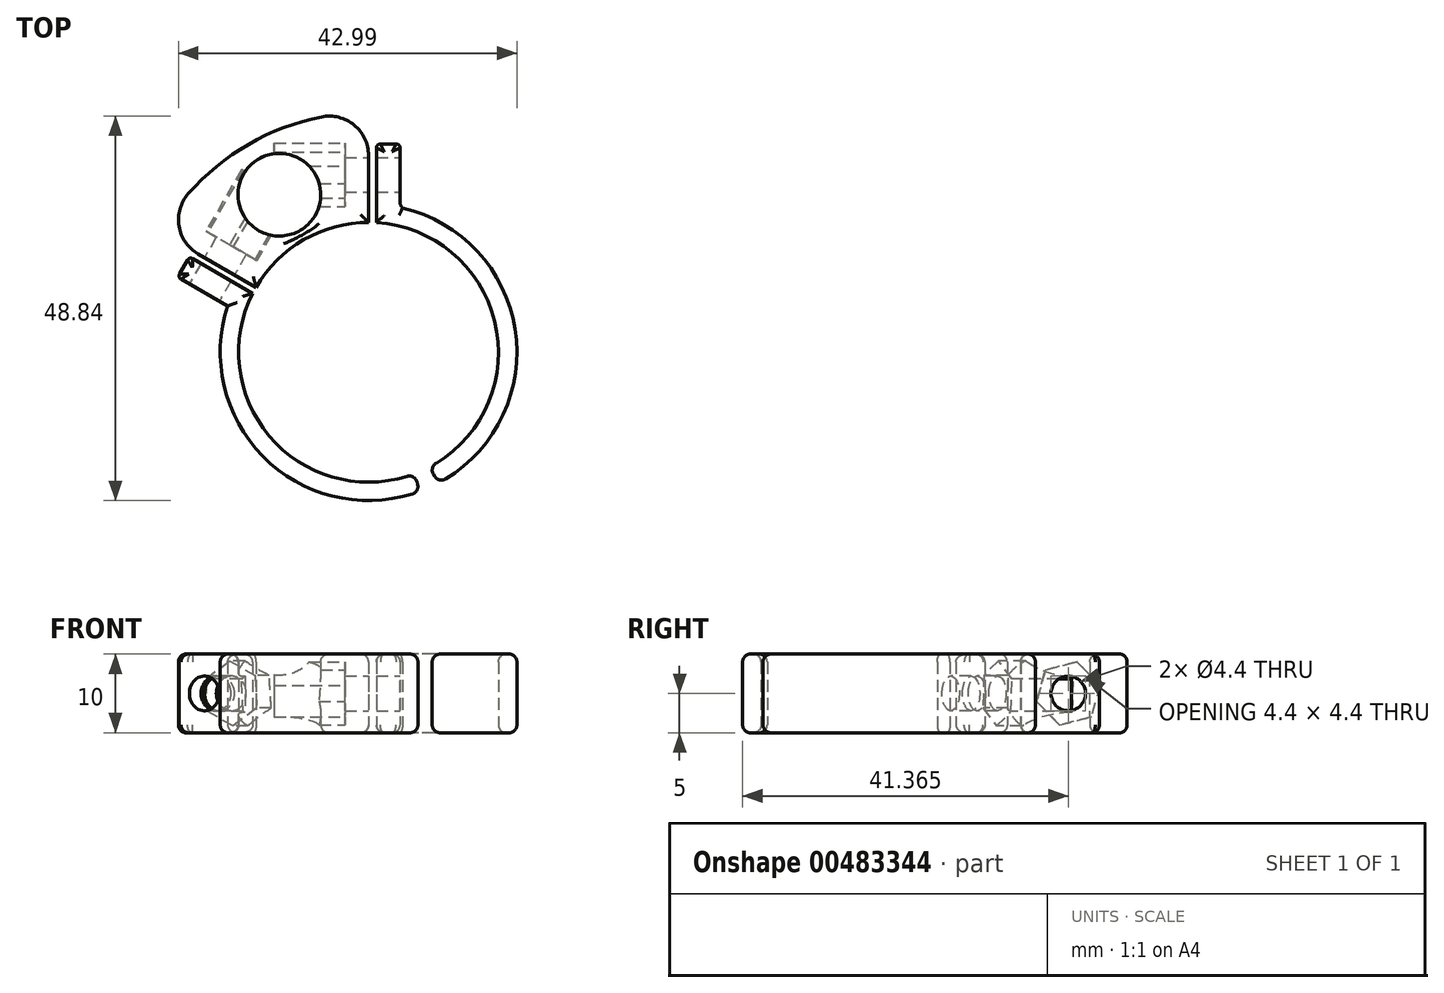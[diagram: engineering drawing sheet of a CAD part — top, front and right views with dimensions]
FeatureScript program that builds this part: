
annotation { "Feature Type Name" : "Feature", "Feature Type Description" : "" }
export const myFeature = defineFeature(function(context is Context, id is Id, definition is map)
    precondition{}
    {
        {
            var Q0;
            Q0=qCreatedBy(makeId("Top.planeOp"),FACE);
            var sketch = newSketch(context, id + "F0", { "sketchPlane" : qUnion([Q0])});
            skLineSegment(sketch, "E0", {"start": v(0, 18.5) * mm, "end": v(0, 18.5) * mm});
            skArc(sketch, "E1", {"start": v(-22.9, 20.13) * mm, "mid": v(-15.25, 26.41) * mm, "end": v(-5.98, 29.9) * mm});
            skLineSegment(sketch, "E2", {"start": v(0, 18.5) * mm, "end": v(0, 25) * mm});
            skLineSegment(sketch, "E3", {"start": v(0, 0) * mm, "end": v(-21.65, 12.5) * mm});
            skLineSegment(sketch, "E4", {"start": v(0, 18.5) * mm, "end": v(0, 24.5) * mm});
            skCircle(sketch, "E5", {"center": v(-11.33, 20.01) * mm, "radius": 5.25 * mm});
            skLineSegment(sketch, "E6", {"start": v(1, 18.47) * mm, "end": v(1, 18.47) * mm});
            skLineSegment(sketch, "E7", {"start": v(1, 18.47) * mm, "end": v(1, 25.97) * mm});
            skLineSegment(sketch, "E8", {"start": v(0, 16.5) * mm, "end": v(0, 18.5) * mm});
            skLineSegment(sketch, "E9", {"start": v(1, 18.47) * mm, "end": v(1, 16.47) * mm});
            skArc(sketch, "E10", {"start": v(0, 16.5) * mm, "mid": v(-8.25, 14.29) * mm, "end": v(-14.29, 8.25) * mm});
            skLineSegment(sketch, "E11", {"start": v(1.5, 26.47) * mm, "end": v(3.5, 26.47) * mm});
            skLineSegment(sketch, "E12", {"start": v(4, 25.97) * mm, "end": v(4, 19.08) * mm});
            skLineSegment(sketch, "E13", {"start": v(-14.7, 7.5) * mm, "end": v(-22.32, 11.9) * mm});
            skLineSegment(sketch, "E14", {"start": v(-23, 11.71) * mm, "end": v(-24, 9.98) * mm});
            skLineSegment(sketch, "E15", {"start": v(-23.82, 9.3) * mm, "end": v(-17.9, 5.88) * mm});
            skPoint(sketch, "E16.visualSharp", {"position": v(-26.41, 15.25) * mm});
            skArc(sketch, "E16.filletArc", {"start": v(-22.9, 20.13) * mm, "mid": v(-24.08, 16.02) * mm, "end": v(-21.65, 12.5) * mm});
            skPoint(sketch, "E17.visualSharp", {"position": v(0, 30.5) * mm});
            skArc(sketch, "E17.filletArc", {"start": v(0, 25) * mm, "mid": v(-1.83, 28.87) * mm, "end": v(-5.98, 29.9) * mm});
            skPoint(sketch, "E18.visualSharp", {"position": v(1, 26.47) * mm});
            skArc(sketch, "E18.filletArc", {"start": v(1.5, 26.47) * mm, "mid": v(1.15, 26.32) * mm, "end": v(1, 25.97) * mm});
            skPoint(sketch, "E19.visualSharp", {"position": v(4, 26.47) * mm});
            skArc(sketch, "E19.filletArc", {"start": v(4, 25.97) * mm, "mid": v(3.85, 26.32) * mm, "end": v(3.5, 26.47) * mm});
            skPoint(sketch, "E20.visualSharp", {"position": v(-24.26, 9.55) * mm});
            skArc(sketch, "E20.filletArc", {"start": v(-24, 9.98) * mm, "mid": v(-24.06, 9.6) * mm, "end": v(-23.82, 9.3) * mm});
            skPoint(sketch, "E21.visualSharp", {"position": v(-22.76, 12.14) * mm});
            skArc(sketch, "E21.filletArc", {"start": v(-22.32, 11.9) * mm, "mid": v(-22.7, 11.94) * mm, "end": v(-23, 11.71) * mm});
            skPoint(sketch, "E22.visualSharp", {"position": v(4, 18.25) * mm});
            skArc(sketch, "E22.filletArc", {"start": v(4, 19.08) * mm, "mid": v(4.22, 18.45) * mm, "end": v(4.8, 18.1) * mm});
            skLineSegment(sketch, "E23", {"start": v(8.9, -16.6) * mm, "end": v(7.7, -14.59) * mm});
            skLineSegment(sketch, "E24", {"start": v(5.85, -15.43) * mm, "end": v(6.49, -17.7) * mm});
            skArc(sketch, "E25", {"start": v(-17.9, 5.88) * mm, "mid": v(-13.1, -13.55) * mm, "end": v(6.49, -17.7) * mm});
            skArc(sketch, "E26.trimOffspring", {"start": v(8.9, -16.6) * mm, "mid": v(18.68, 2.45) * mm, "end": v(4.33, 18.34) * mm});
            skArc(sketch, "E27", {"start": v(1, 16.47) * mm, "mid": v(16.13, 3.48) * mm, "end": v(7.7, -14.59) * mm});
            skArc(sketch, "E28", {"start": v(5.85, -15.43) * mm, "mid": v(-12.29, -11.01) * mm, "end": v(-14.7, 7.5) * mm});
            skSolve(sketch);
        }
        {
            var Q0;
            Q0=qSketchRegion(id+"F0",true);
            extrude(context, id + "F1", {"entities" : qUnion([Q0]), "depth" : 10 * mm});
        }
        {
            var Q0;
            Q0=makeQuery(id+"F1.opExtrude","SWEPT_FACE",FACE,{"disambiguationData":[OSD([sQuery(id+"F0.wireOp",EDGE,"E12")])]});
            var sketch = newSketch(context, id + "F2", { "sketchPlane" : qUnion([Q0])});
            skCircle(sketch, "E29", {"center": v(22.52, 5) * mm, "radius": 2.2 * mm});
            skPoint(sketch, "E29.centerSnap0", {"position": v(22.52, 0) * mm});
            skPoint(sketch, "E29.centerSnap1", {"position": v(19.08, 5) * mm});
            skSolve(sketch);
        }
        {
            var Q0;
            Q0=qSketchRegion(id+"F2",true);
            extrude(context, id + "F3", {"entities" : qUnion([Q0]), "operationType" : NewBodyOperationType.REMOVE, "oppositeDirection" : true, "depth" : 8 * mm});
        }
        {
            var Q0;
            Q0=makeQuery(id+"F1.opExtrude","SWEPT_FACE",FACE,{"disambiguationData":[OSD([sQuery(id+"F0.wireOp",EDGE,"E15")])]});
            var sketch = newSketch(context, id + "F4", { "sketchPlane" : qUnion([Q0])});
            skCircle(sketch, "E30", {"center": v(-21.86, 5) * mm, "radius": 2.2 * mm});
            skPoint(sketch, "E30.centerSnap0", {"position": v(-21.86, 10) * mm});
            skPoint(sketch, "E30.centerSnap1", {"position": v(-25.28, 5) * mm});
            skSolve(sketch);
        }
        {
            var Q0;
            Q0=makeQuery(id+"F4.imprint","IMPRINT",FACE,{"disambiguationData":[TD([[makeQuery(id+"F4.imprint","IMPRINT",EDGE,{"derivedFrom":sQuery(id+"F4.wireOp",EDGE,"E30")}),1.0]])]});
            extrude(context, id + "F5", {"entities" : qUnion([Q0]), "operationType" : NewBodyOperationType.REMOVE, "oppositeDirection" : true, "depth" : 10 * mm});
        }
        {
            var Q0;
            Q0=makeQuery(id+"F1.opExtrude","SWEPT_FACE",FACE,{"disambiguationData":[OSD([sQuery(id+"F0.wireOp",EDGE,"E3")])]});
            var sketch = newSketch(context, id + "F6", { "sketchPlane" : qUnion([Q0])});
            skCircle(sketch, "E31.cCircle", {"center": v(-21.86, 5) * mm, "radius": 3.6 * mm, "construction": true});
            skLineSegment(sketch, "E31.0", {"start": v(-22.11, 9.15) * mm, "end": v(-18.4, 7.3) * mm});
            skLineSegment(sketch, "E31.1", {"start": v(-18.4, 7.3) * mm, "end": v(-18.14, 3.14) * mm});
            skLineSegment(sketch, "E31.2", {"start": v(-18.14, 3.14) * mm, "end": v(-21.6, 0.85) * mm});
            skLineSegment(sketch, "E31.3", {"start": v(-21.6, 0.85) * mm, "end": v(-25.33, 2.7) * mm});
            skLineSegment(sketch, "E31.4", {"start": v(-25.33, 2.7) * mm, "end": v(-25.58, 6.86) * mm});
            skLineSegment(sketch, "E31.5", {"start": v(-25.58, 6.86) * mm, "end": v(-22.11, 9.15) * mm});
            skPoint(sketch, "E31.0.midPoint", {"position": v(-20.25, 8.22) * mm});
            skSolve(sketch);
        }
        {
            var Q0;
            Q0=makeQuery(id+"F6.imprint","IMPRINT",FACE,{"disambiguationData":[TD([[makeQuery(id+"F6.imprint","IMPRINT",EDGE,{"derivedFrom":makeQuery(id+"F5.boolean.opBoolean","INTERSECT",EDGE,{"derivedFrom":[makeQuery(id+"F1.opExtrude","SWEPT_FACE",FACE,{"disambiguationData":[OSD([sQuery(id+"F0.wireOp",EDGE,"E3")])]}),makeQuery(id+"F5.opExtrude","SWEPT_FACE",FACE,{"disambiguationData":[OSD([sQuery(id+"F4.wireOp",EDGE,"E30")])]})]})}),1.0]])]});
            var Q1;
            {var subQ0=sQuery(id+"F6.wireOp",EDGE,"E31.4");Q1=makeQuery(id+"F6.imprint","IMPRINT",FACE,{"disambiguationData":[TD([[makeQuery(id+"F6.imprint","IMPRINT",EDGE,{"derivedFrom":subQ0}),-1.0]])]});}
            var Q2;
            {var subQ7=sQuery(id+"F6.wireOp",EDGE,"E31.0");Q2=makeQuery(id+"F6.imprint","IMPRINT",FACE,{"disambiguationData":[TD([[makeQuery(id+"F6.imprint","IMPRINT",EDGE,{"derivedFrom":subQ7}),-1.0]])]});}
            extrude(context, id + "F7", {"entities" : qUnion([Q0, Q1, Q2]), "operationType" : NewBodyOperationType.REMOVE, "oppositeDirection" : true, "depth" : 12 * mm, "hasSecondDirection" : true, "secondDirectionOppositeDirection" : true, "secondDirectionDepth" : 3 * mm});
        }
        {
            var Q0;
            Q0=makeQuery(id+"F1.opExtrude","SWEPT_FACE",FACE,{"disambiguationData":[OSD([sQuery(id+"F0.wireOp",EDGE,"E2"),sQuery(id+"F0.wireOp",EDGE,"E4"),sQuery(id+"F0.wireOp",EDGE,"E8")])]});
            var sketch = newSketch(context, id + "F8", { "sketchPlane" : qUnion([Q0])});
            skCircle(sketch, "E32.cCircle", {"center": v(22.52, 5) * mm, "radius": 3.6 * mm, "construction": true});
            skLineSegment(sketch, "E32.0", {"start": v(19.62, 7.97) * mm, "end": v(23.64, 9) * mm});
            skLineSegment(sketch, "E32.1", {"start": v(23.64, 9) * mm, "end": v(26.55, 6.03) * mm});
            skLineSegment(sketch, "E32.2", {"start": v(26.55, 6.03) * mm, "end": v(25.43, 2.03) * mm});
            skLineSegment(sketch, "E32.3", {"start": v(25.43, 2.03) * mm, "end": v(21.4, 1) * mm});
            skLineSegment(sketch, "E32.4", {"start": v(21.4, 1) * mm, "end": v(18.5, 3.97) * mm});
            skLineSegment(sketch, "E32.5", {"start": v(18.5, 3.97) * mm, "end": v(19.62, 7.97) * mm});
            skPoint(sketch, "E32.0.midPoint", {"position": v(21.63, 8.49) * mm});
            skSolve(sketch);
        }
        {
            var Q0;
            Q0=qSketchRegion(id+"F8",true);
            extrude(context, id + "F9", {"entities" : qUnion([Q0]), "operationType" : NewBodyOperationType.REMOVE, "oppositeDirection" : true, "depth" : 12 * mm, "hasSecondDirection" : true, "secondDirectionOppositeDirection" : true, "secondDirectionDepth" : 3 * mm});
        }
        {
            var Q0;
            Q0=makeQuery(id+"F1.opExtrude","SWEPT_FACE",FACE,{"disambiguationData":[OSD([sQuery(id+"F0.wireOp",EDGE,"E24")])]});
            var Q1;
            Q1=makeQuery(id+"F1.opExtrude","SWEPT_FACE",FACE,{"disambiguationData":[OSD([sQuery(id+"F0.wireOp",EDGE,"E23")])]});
            var Q2;
            Q2=makeQuery(id+"F1.opExtrude","CAP_FACE",FACE,{"disambiguationData":[OSD([sQuery(id+"F0.wireOp",EDGE,"E13"),sQuery(id+"F0.wireOp",EDGE,"E14"),sQuery(id+"F0.wireOp",EDGE,"E15"),sQuery(id+"F0.wireOp",EDGE,"E20.filletArc"),sQuery(id+"F0.wireOp",EDGE,"E21.filletArc"),sQuery(id+"F0.wireOp",EDGE,"E24"),sQuery(id+"F0.wireOp",EDGE,"E25"),sQuery(id+"F0.wireOp",EDGE,"a188417b-cc8c-4509-bfe6-a5d54d56d6b7.trimOffspring")])],"isStart":false});
            var Q3;
            Q3=makeQuery(id+"F1.opExtrude","CAP_FACE",FACE,{"disambiguationData":[OSD([sQuery(id+"F0.wireOp",EDGE,"E7"),sQuery(id+"F0.wireOp",EDGE,"E9"),sQuery(id+"F0.wireOp",EDGE,"E11"),sQuery(id+"F0.wireOp",EDGE,"E12"),sQuery(id+"F0.wireOp",EDGE,"E18.filletArc"),sQuery(id+"F0.wireOp",EDGE,"E19.filletArc"),sQuery(id+"F0.wireOp",EDGE,"E22.filletArc"),sQuery(id+"F0.wireOp",EDGE,"E23"),sQuery(id+"F0.wireOp",EDGE,"jDdMIHg0-1Oi0-MaQn-ggq3-3935tTYizpBS"),sQuery(id+"F0.wireOp",EDGE,"E26.trimOffspring")])],"isStart":false});
            var Q4;
            Q4=makeQuery(id+"F1.opExtrude","CAP_FACE",FACE,{"disambiguationData":[OSD([sQuery(id+"F0.wireOp",EDGE,"E1"),sQuery(id+"F0.wireOp",EDGE,"E2"),sQuery(id+"F0.wireOp",EDGE,"E3"),sQuery(id+"F0.wireOp",EDGE,"E4"),sQuery(id+"F0.wireOp",EDGE,"E5"),sQuery(id+"F0.wireOp",EDGE,"E8"),sQuery(id+"F0.wireOp",EDGE,"E10"),sQuery(id+"F0.wireOp",EDGE,"E16.filletArc"),sQuery(id+"F0.wireOp",EDGE,"E17.filletArc")])],"isStart":false});
            var Q5;
            Q5=makeQuery(id+"F1.opExtrude","CAP_FACE",FACE,{"disambiguationData":[OSD([sQuery(id+"F0.wireOp",EDGE,"E1"),sQuery(id+"F0.wireOp",EDGE,"E2"),sQuery(id+"F0.wireOp",EDGE,"E3"),sQuery(id+"F0.wireOp",EDGE,"E4"),sQuery(id+"F0.wireOp",EDGE,"E5"),sQuery(id+"F0.wireOp",EDGE,"E8"),sQuery(id+"F0.wireOp",EDGE,"E10"),sQuery(id+"F0.wireOp",EDGE,"E16.filletArc"),sQuery(id+"F0.wireOp",EDGE,"E17.filletArc")])],"isStart":true});
            var Q6;
            Q6=makeQuery(id+"F1.opExtrude","CAP_FACE",FACE,{"disambiguationData":[OSD([sQuery(id+"F0.wireOp",EDGE,"E7"),sQuery(id+"F0.wireOp",EDGE,"E9"),sQuery(id+"F0.wireOp",EDGE,"E11"),sQuery(id+"F0.wireOp",EDGE,"E12"),sQuery(id+"F0.wireOp",EDGE,"E18.filletArc"),sQuery(id+"F0.wireOp",EDGE,"E19.filletArc"),sQuery(id+"F0.wireOp",EDGE,"E22.filletArc"),sQuery(id+"F0.wireOp",EDGE,"E23"),sQuery(id+"F0.wireOp",EDGE,"jDdMIHg0-1Oi0-MaQn-ggq3-3935tTYizpBS"),sQuery(id+"F0.wireOp",EDGE,"E26.trimOffspring")])],"isStart":true});
            var Q7;
            Q7=makeQuery(id+"F1.opExtrude","CAP_FACE",FACE,{"disambiguationData":[OSD([sQuery(id+"F0.wireOp",EDGE,"E13"),sQuery(id+"F0.wireOp",EDGE,"E14"),sQuery(id+"F0.wireOp",EDGE,"E15"),sQuery(id+"F0.wireOp",EDGE,"E20.filletArc"),sQuery(id+"F0.wireOp",EDGE,"E21.filletArc"),sQuery(id+"F0.wireOp",EDGE,"E24"),sQuery(id+"F0.wireOp",EDGE,"E25"),sQuery(id+"F0.wireOp",EDGE,"a188417b-cc8c-4509-bfe6-a5d54d56d6b7.trimOffspring")])],"isStart":true});
            fillet(context, id + "F10", {"entities" : qUnion([Q0, Q1, Q2, Q3, Q4, Q5, Q6, Q7]), "radius" : 1 * mm, "tangentPropagation" : true, "allowEdgeOverflow" : false});
        }
    });
